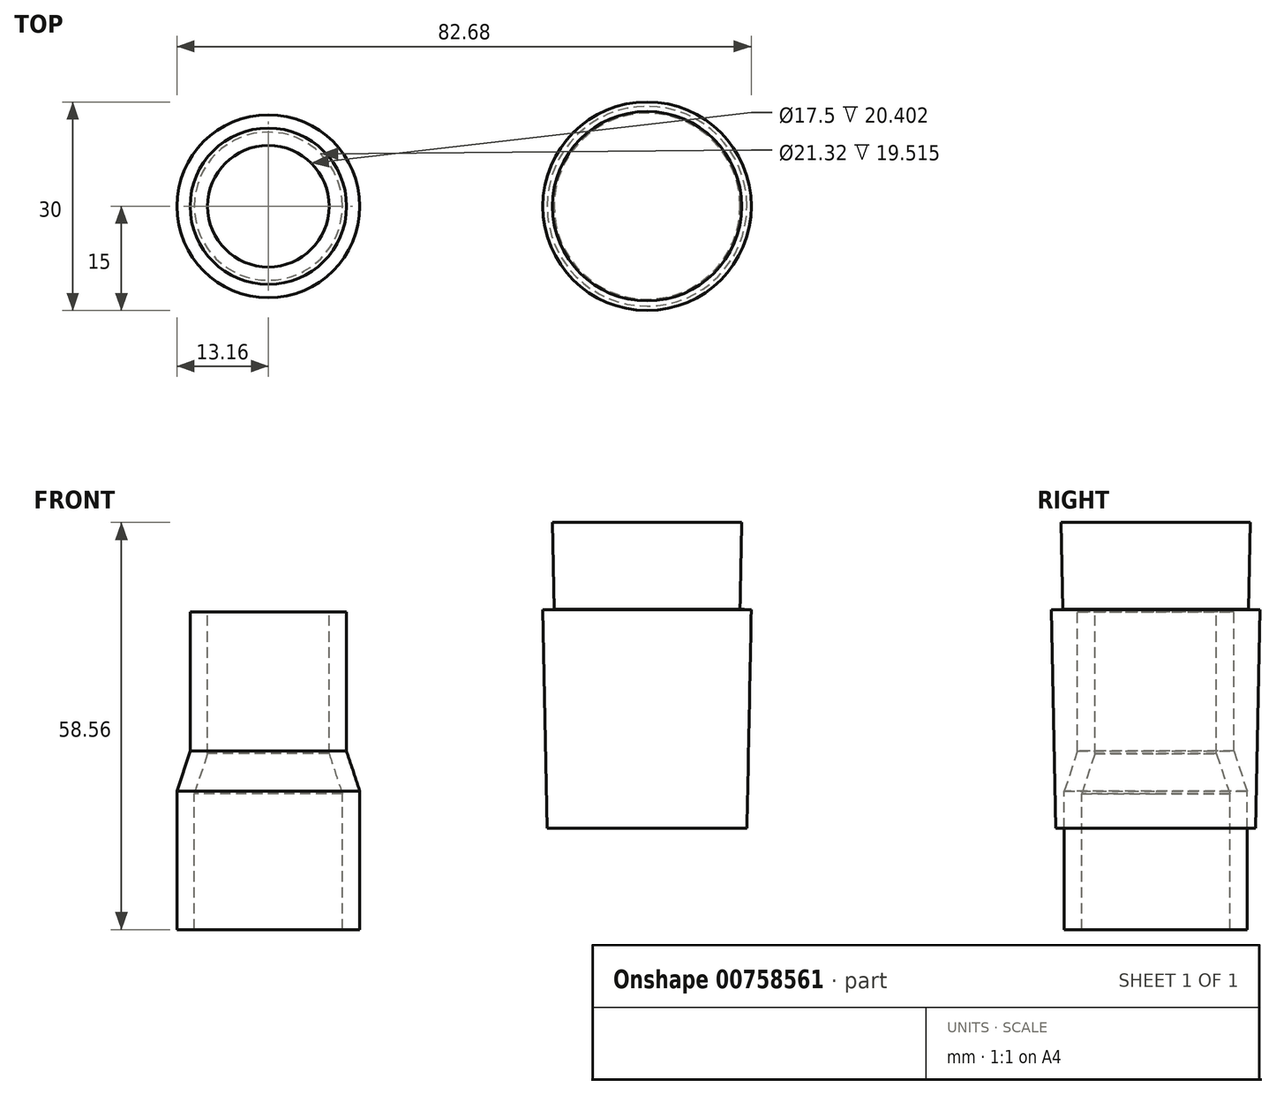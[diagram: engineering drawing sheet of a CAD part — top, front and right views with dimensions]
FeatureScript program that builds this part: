
annotation { "Feature Type Name" : "Feature", "Feature Type Description" : "" }
export const myFeature = defineFeature(function(context is Context, id is Id, definition is map)
    precondition{}
    {
        {
            var Q0;
            Q0=qCreatedBy(makeId("Front.planeOp"),FACE);
            var sketch = newSketch(context, id + "F0", { "sketchPlane" : qUnion([Q0])});
            skLineSegment(sketch, "E0", {"start": v(11.25, 45.7) * mm, "end": v(11.25, 25.7) * mm});
            skLineSegment(sketch, "E1", {"start": v(11.25, 25.7) * mm, "end": v(13.16, 19.92) * mm});
            skLineSegment(sketch, "E2", {"start": v(13.16, 19.92) * mm, "end": v(13.16, 0) * mm});
            skLineSegment(sketch, "E3", {"start": v(13.16, 0) * mm, "end": v(10.66, 0) * mm});
            skLineSegment(sketch, "E4.0", {"start": v(10.66, 19.51) * mm, "end": v(10.66, 0) * mm});
            skLineSegment(sketch, "E4.1", {"start": v(8.75, 25.3) * mm, "end": v(10.66, 19.51) * mm});
            skLineSegment(sketch, "E4.2", {"start": v(8.75, 45.7) * mm, "end": v(8.75, 25.3) * mm});
            skLineSegment(sketch, "E5.trimOffspring", {"start": v(8.75, 45.7) * mm, "end": v(11.25, 45.7) * mm});
            skLineSegment(sketch, "E6", {"start": v(0, 62.04) * mm, "end": v(0, -14.67) * mm, "construction": true});
            skLineSegment(sketch, "E7", {"start": v(40.14, 14.56) * mm, "end": v(54.52, 14.56) * mm});
            skLineSegment(sketch, "E8", {"start": v(40.9, 58.56) * mm, "end": v(54.52, 58.56) * mm});
            skLineSegment(sketch, "E9", {"start": v(40.9, 58.56) * mm, "end": v(41.14, 46.06) * mm});
            skLineSegment(sketch, "E10", {"start": v(54.52, 76.28) * mm, "end": v(54.52, 2.76) * mm, "construction": true});
            skPoint(sketch, "E11.orphan", {"position": v(54.52, 58.56) * mm});
            skLineSegment(sketch, "E12", {"start": v(40.14, 14.56) * mm, "end": v(39.51, 46.03) * mm});
            skLineSegment(sketch, "E13", {"start": v(41.14, 46.06) * mm, "end": v(39.51, 46.03) * mm});
            skPoint(sketch, "E13.endSnap0", {"position": v(39.51, 46.03) * mm});
            skPoint(sketch, "E14.orphan", {"position": v(38.88, 77.5) * mm});
            skPoint(sketch, "E15.orphan", {"position": v(68.14, 58.56) * mm});
            skLineSegment(sketch, "E16", {"start": v(54.52, 58.56) * mm, "end": v(54.52, 14.56) * mm});
            skSolve(sketch);
        }
        {
            var Q0;
            Q0=makeQuery(id+"F0.imprint","IMPRINT",FACE,{"disambiguationData":[TD([[makeQuery(id+"F0.imprint","IMPRINT",EDGE,{"derivedFrom":sQuery(id+"F0.wireOp",EDGE,"E0")}),-1.0]])]});
            var Q1;
            Q1=sQuery(id+"F0.wireOp",EDGE,"E6");
            revolve(context, id + "F1", {"surfaceOperationType" : NewSurfaceOperationType.NEW, "entities" : qUnion([Q0]), "axis" : qUnion([Q1]), "revolveType" : RevolveType.FULL});
        }
        {
            var Q0;
            Q0=makeQuery(id+"F0.imprint","IMPRINT",FACE,{"disambiguationData":[TD([[makeQuery(id+"F0.imprint","IMPRINT",EDGE,{"derivedFrom":sQuery(id+"F0.wireOp",EDGE,"E7")}),1.0]])]});
            var Q1;
            Q1=sQuery(id+"F0.wireOp",EDGE,"E10");
            revolve(context, id + "F2", {"surfaceOperationType" : NewSurfaceOperationType.NEW, "entities" : qUnion([Q0]), "axis" : qUnion([Q1]), "revolveType" : RevolveType.FULL});
        }
    });
